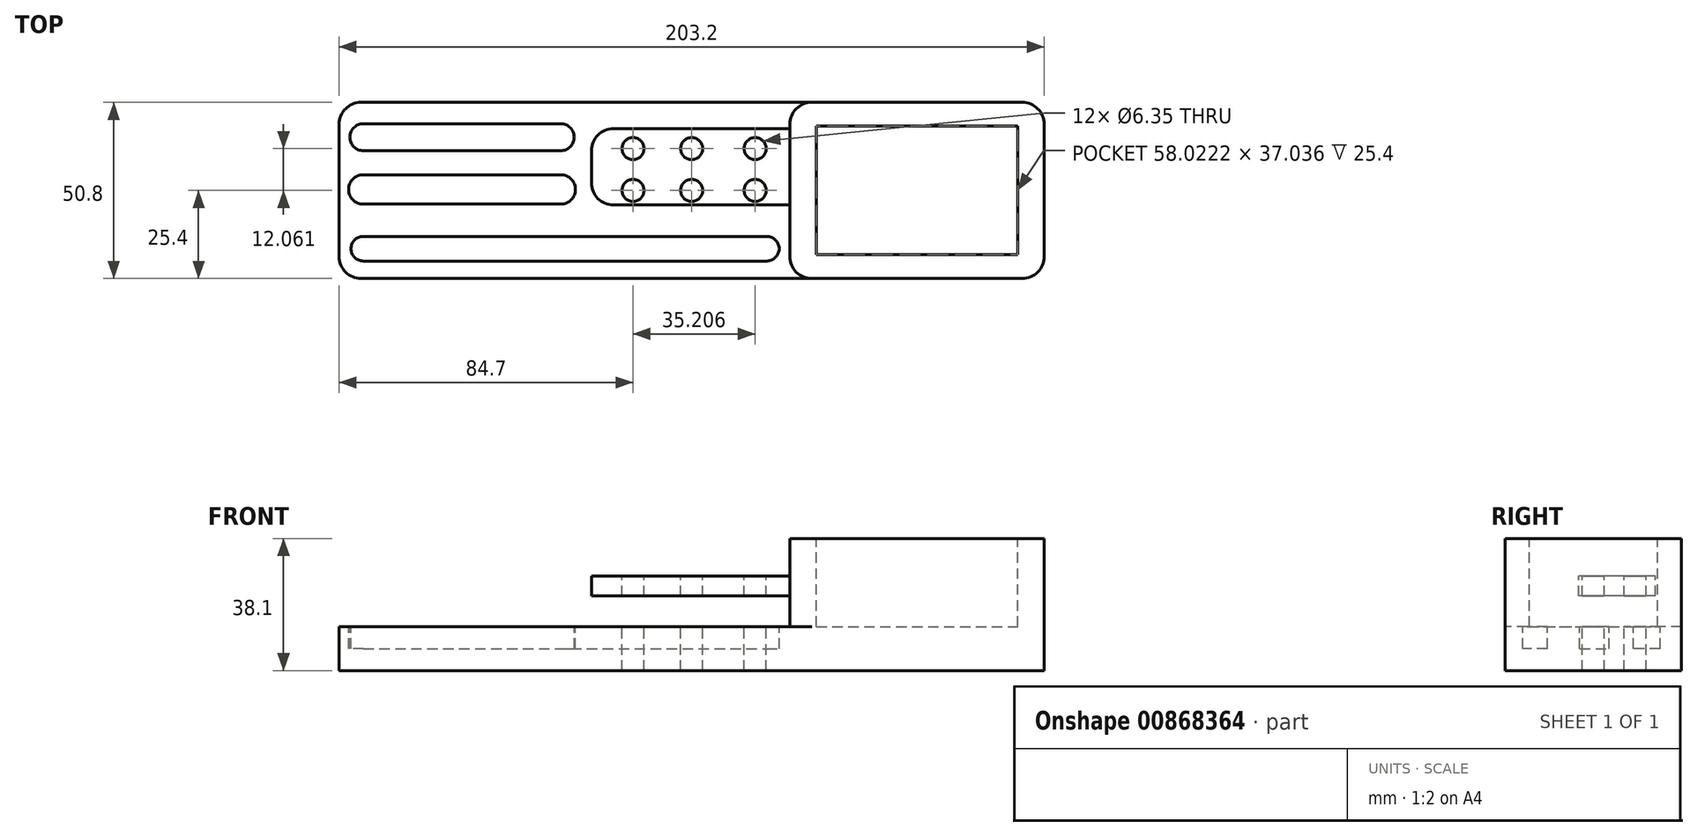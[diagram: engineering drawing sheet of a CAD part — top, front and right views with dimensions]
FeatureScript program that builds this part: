
annotation { "Feature Type Name" : "Feature", "Feature Type Description" : "" }
export const myFeature = defineFeature(function(context is Context, id is Id, definition is map)
    precondition{}
    {
        {
            var Q0;
            Q0=qCreatedBy(makeId("Top.planeOp"),FACE);
            var sketch = newSketch(context, id + "F0", { "sketchPlane" : qUnion([Q0])});
            skLineSegment(sketch, "E0.bottom", {"start": v(-101.6, -25.4) * mm, "end": v(101.6, -25.4) * mm});
            skLineSegment(sketch, "E0.top", {"start": v(-101.6, 25.4) * mm, "end": v(101.6, 25.4) * mm});
            skLineSegment(sketch, "E0.left", {"start": v(-101.6, -25.4) * mm, "end": v(-101.6, 25.4) * mm});
            skLineSegment(sketch, "E0.right", {"start": v(101.6, -25.4) * mm, "end": v(101.6, 25.4) * mm});
            skPoint(sketch, "E0.middle", {"position": v(0, 0) * mm});
            skLineSegment(sketch, "E1", {"start": v(45.35, 25.4) * mm, "end": v(45.35, -25.4) * mm});
            skSolve(sketch);
        }
        {
            var Q0;
            {var subQ0=sQuery(id+"F0.wireOp",EDGE,"E0.left");Q0=makeQuery(id+"F0.imprint","IMPRINT",FACE,{"disambiguationData":[TD([[makeQuery(id+"F0.imprint","IMPRINT",EDGE,{"derivedFrom":subQ0}),-1.0]])]});}
            var Q1;
            {var subQ0=sQuery(id+"F0.wireOp",EDGE,"E0.right");Q1=makeQuery(id+"F0.imprint","IMPRINT",FACE,{"disambiguationData":[TD([[makeQuery(id+"F0.imprint","IMPRINT",EDGE,{"derivedFrom":subQ0}),1.0]])]});}
            extrude(context, id + "F1", {"entities" : qUnion([Q0, Q1]), "depth" : 12.7 * mm, "offsetDistance" : 25.4 * mm});
        }
        {
            var Q0;
            Q0=makeQuery(id+"F1.opExtrude","CAP_FACE",FACE,{"disambiguationData":[OSD([sQuery(id+"F0.wireOp",EDGE,"E0.bottom"),sQuery(id+"F0.wireOp",EDGE,"E0.top"),sQuery(id+"F0.wireOp",EDGE,"E0.left"),sQuery(id+"F0.wireOp",EDGE,"E0.right")])],"isStart":false});
            var sketch = newSketch(context, id + "F2", { "sketchPlane" : qUnion([Q0])});
            skLineSegment(sketch, "E2", {"start": v(28.28, 25.4) * mm, "end": v(28.28, -25.4) * mm});
            skLineSegment(sketch, "E3", {"start": v(28.28, -25.4) * mm, "end": v(101.6, -25.4) * mm});
            skLineSegment(sketch, "E4", {"start": v(101.6, -25.4) * mm, "end": v(101.6, 25.4) * mm});
            skLineSegment(sketch, "E5", {"start": v(101.6, 25.4) * mm, "end": v(28.28, 25.4) * mm});
            skSolve(sketch);
        }
        {
            var Q0;
            Q0 = qSketchRegion(id + "F2", true);
            extrude(context, id + "F3", {"entities" : qUnion([Q0]), "operationType" : NewBodyOperationType.ADD, "depth" : 25.4 * mm, "offsetDistance" : 25.4 * mm});
        }
        {
            var Q0;
            Q0=makeQuery(id+"F3.opExtrude","CAP_FACE",FACE,{"disambiguationData":[OSD([sQuery(id+"F2.wireOp",EDGE,"E2"),sQuery(id+"F2.wireOp",EDGE,"E3"),sQuery(id+"F2.wireOp",EDGE,"E4"),sQuery(id+"F2.wireOp",EDGE,"E5")])],"isStart":false});
            var sketch = newSketch(context, id + "F4", { "sketchPlane" : qUnion([Q0])});
            skPoint(sketch, "E6", {"position": v(64.94, 0) * mm});
            skLineSegment(sketch, "E7.bottom", {"start": v(35.93, -18.52) * mm, "end": v(93.95, -18.52) * mm});
            skLineSegment(sketch, "E7.top", {"start": v(35.93, 18.52) * mm, "end": v(93.95, 18.52) * mm});
            skLineSegment(sketch, "E7.left", {"start": v(35.93, -18.52) * mm, "end": v(35.93, 18.52) * mm});
            skLineSegment(sketch, "E7.right", {"start": v(93.95, -18.52) * mm, "end": v(93.95, 18.52) * mm});
            skSolve(sketch);
        }
        {
            var Q0;
            Q0 = qSketchRegion(id + "F4", true);
            extrude(context, id + "F5", {"entities" : qUnion([Q0]), "operationType" : NewBodyOperationType.REMOVE, "oppositeDirection" : true, "depth" : 25.4 * mm, "offsetDistance" : 25.4 * mm});
        }
        {
            var Q0;
            Q0=makeQuery(id+"F1.opExtrude","CAP_FACE",FACE,{"disambiguationData":[OSD([sQuery(id+"F0.wireOp",EDGE,"E0.bottom"),sQuery(id+"F0.wireOp",EDGE,"E0.top"),sQuery(id+"F0.wireOp",EDGE,"E0.left"),sQuery(id+"F0.wireOp",EDGE,"E0.right")])],"isStart":false});
            var sketch = newSketch(context, id + "F6", { "sketchPlane" : qUnion([Q0])});
            skLineSegment(sketch, "E8.bottom", {"start": v(-94.61, 19.25) * mm, "end": v(-37.74, 19.25) * mm});
            skLineSegment(sketch, "E8.top", {"start": v(-94.61, 11.46) * mm, "end": v(-37.74, 11.46) * mm});
            skLineSegment(sketch, "E9.bottom", {"start": v(-94.61, 4.52) * mm, "end": v(-37.74, 4.52) * mm});
            skLineSegment(sketch, "E9.top", {"start": v(-94.61, -3.94) * mm, "end": v(-37.74, -3.94) * mm});
            skLineSegment(sketch, "E10.bottom", {"start": v(-94.61, -13.25) * mm, "end": v(21.67, -13.25) * mm});
            skLineSegment(sketch, "E10.top", {"start": v(-94.61, -20.36) * mm, "end": v(21.67, -20.36) * mm});
            skArc(sketch, "E11", {"start": v(-94.61, 19.25) * mm, "mid": v(-98.5, 15.35) * mm, "end": v(-94.61, 11.46) * mm});
            skArc(sketch, "E12", {"start": v(-37.74, 11.46) * mm, "mid": v(-33.85, 15.35) * mm, "end": v(-37.74, 19.25) * mm});
            skArc(sketch, "E13", {"start": v(-37.74, -3.94) * mm, "mid": v(-33.5, 0.29) * mm, "end": v(-37.74, 4.52) * mm});
            skArc(sketch, "E14", {"start": v(-94.61, 4.52) * mm, "mid": v(-98.84, 0.29) * mm, "end": v(-94.61, -3.94) * mm});
            skArc(sketch, "E15", {"start": v(-94.61, -13.25) * mm, "mid": v(-98.17, -16.8) * mm, "end": v(-94.61, -20.36) * mm});
            skArc(sketch, "E16", {"start": v(21.67, -20.36) * mm, "mid": v(25.22, -16.8) * mm, "end": v(21.67, -13.25) * mm});
            skSolve(sketch);
        }
        {
            var Q0;
            Q0 = qSketchRegion(id + "F6", true);
            extrude(context, id + "F7", {"entities" : qUnion([Q0]), "operationType" : NewBodyOperationType.REMOVE, "oppositeDirection" : true, "depth" : 6.35 * mm, "offsetDistance" : 25.4 * mm});
        }
        {
            var Q0;
            Q0=makeQuery(id+"F3.opExtrude","SWEPT_EDGE",EDGE,{"disambiguationData":[OSD([sQuery(id+"F0.wireOp",EDGE,"E0.bottom"),sQuery(id+"F2.wireOp",EDGE,"E2"),sQuery(id+"F2.wireOp",EDGE,"E3")])]});
            var Q1;
            Q1=makeQuery(id+"F3.opExtrude","SWEPT_EDGE",EDGE,{"disambiguationData":[OSD([sQuery(id+"F0.wireOp",EDGE,"E0.top"),sQuery(id+"F2.wireOp",EDGE,"E2"),sQuery(id+"F2.wireOp",EDGE,"E5")])]});
            var Q2;
            Q2=makeQuery(id+"F1.opExtrude","SWEPT_EDGE",EDGE,{"disambiguationData":[OSD([sQuery(id+"F0.wireOp",EDGE,"E0.bottom"),sQuery(id+"F0.wireOp",EDGE,"E0.left")])]});
            var Q3;
            Q3=makeQuery(id+"F1.opExtrude","SWEPT_EDGE",EDGE,{"disambiguationData":[OSD([sQuery(id+"F0.wireOp",EDGE,"E0.top"),sQuery(id+"F0.wireOp",EDGE,"E0.left")])]});
            var Q4;
            Q4=makeQuery(id+"F3.boolean.opBoolean","MERGE",EDGE,{"derivedFrom":[makeQuery(id+"F1.opExtrude","SWEPT_EDGE",EDGE,{"disambiguationData":[OSD([sQuery(id+"F0.wireOp",EDGE,"E0.top"),sQuery(id+"F0.wireOp",EDGE,"E0.right")])]}),makeQuery(id+"F3.opExtrude","SWEPT_EDGE",EDGE,{"disambiguationData":[OSD([sQuery(id+"F2.wireOp",EDGE,"E4"),sQuery(id+"F2.wireOp",EDGE,"E5")])]})]});
            var Q5;
            Q5=makeQuery(id+"F3.boolean.opBoolean","MERGE",EDGE,{"derivedFrom":[makeQuery(id+"F1.opExtrude","SWEPT_EDGE",EDGE,{"disambiguationData":[OSD([sQuery(id+"F0.wireOp",EDGE,"E0.bottom"),sQuery(id+"F0.wireOp",EDGE,"E0.right")])]}),makeQuery(id+"F3.opExtrude","SWEPT_EDGE",EDGE,{"disambiguationData":[OSD([sQuery(id+"F2.wireOp",EDGE,"E3"),sQuery(id+"F2.wireOp",EDGE,"E4")])]})]});
            fillet(context, id + "F8", {"entities" : qUnion([Q0, Q1, Q2, Q3, Q4, Q5]), "radius" : 6.35 * mm, "tangentPropagation" : true, "allowEdgeOverflow" : false});
        }
        {
            var Q0;
            Q0=makeQuery(id+"F3.opExtrude","SWEPT_FACE",FACE,{"disambiguationData":[OSD([sQuery(id+"F2.wireOp",EDGE,"E2")])]});
            var sketch = newSketch(context, id + "F9", { "sketchPlane" : qUnion([Q0])});
            skLineSegment(sketch, "E17.bottom", {"start": v(-17.81, 21.53) * mm, "end": v(4.19, 21.53) * mm});
            skLineSegment(sketch, "E17.top", {"start": v(-17.81, 27.28) * mm, "end": v(4.19, 27.28) * mm});
            skLineSegment(sketch, "E17.left", {"start": v(-17.81, 21.53) * mm, "end": v(-17.81, 27.28) * mm});
            skLineSegment(sketch, "E17.right", {"start": v(4.19, 21.53) * mm, "end": v(4.19, 27.28) * mm});
            skPoint(sketch, "E17.middle", {"position": v(-6.81, 24.4) * mm});
            skSolve(sketch);
        }
        {
            var Q0;
            Q0 = qSketchRegion(id + "F9", true);
            extrude(context, id + "F10", {"entities" : qUnion([Q0]), "operationType" : NewBodyOperationType.ADD, "depth" : 57.15 * mm, "offsetDistance" : 25.4 * mm});
        }
        {
            var Q0;
            Q0=makeQuery(id+"F10.opExtrude","CAP_EDGE",EDGE,{"disambiguationData":[OSD([sQuery(id+"F9.wireOp",EDGE,"E17.right")])],"isStart":false});
            var Q1;
            Q1=makeQuery(id+"F10.opExtrude","CAP_EDGE",EDGE,{"disambiguationData":[OSD([sQuery(id+"F9.wireOp",EDGE,"E17.left")])],"isStart":false});
            fillet(context, id + "F11", {"entities" : qUnion([Q0, Q1]), "radius" : 6.35 * mm, "tangentPropagation" : true, "allowEdgeOverflow" : false});
        }
        {
            var Q0;
            Q0=makeQuery(id+"F10.opExtrude","SWEPT_FACE",FACE,{"disambiguationData":[OSD([sQuery(id+"F9.wireOp",EDGE,"E17.top")])]});
            var sketch = newSketch(context, id + "F12", { "sketchPlane" : qUnion([Q0])});
            skPoint(sketch, "E18", {"position": v(-16.9, 12.06) * mm});
            skPoint(sketch, "E19", {"position": v(0, 12.06) * mm});
            skPoint(sketch, "E20", {"position": v(18.3, 12.06) * mm});
            skPoint(sketch, "E21", {"position": v(18.3, 0) * mm});
            skPoint(sketch, "E22", {"position": v(0, 0) * mm});
            skPoint(sketch, "E23", {"position": v(-16.9, 0) * mm});
            skSolve(sketch);
        }
        {
            var Q0;
            Q0=sQuery(id+"F12.wireOp",VERTEX,"E18");
            var Q1;
            Q1=sQuery(id+"F12.wireOp",VERTEX,"E19");
            var Q2;
            Q2=sQuery(id+"F12.wireOp",VERTEX,"E20");
            var Q3;
            Q3=sQuery(id+"F12.wireOp",VERTEX,"E21");
            var Q4;
            Q4=sQuery(id+"F12.wireOp",VERTEX,"E22");
            var Q5;
            Q5=sQuery(id+"F12.wireOp",VERTEX,"E23");
            var Q6;
            Q6=makeQuery(id+"F1.opExtrude","SWEPT_BODY",BODY,{"disambiguationData":[OSD([sQuery(id+"F0.wireOp",EDGE,"E0.bottom"),sQuery(id+"F0.wireOp",EDGE,"E0.top"),sQuery(id+"F0.wireOp",EDGE,"E0.left"),sQuery(id+"F0.wireOp",EDGE,"E0.right")])]});
            hole(context, id + "F13", {"style" : HoleStyle.SIMPLE, "endStyle" : HoleEndStyle.THROUGH, "holeDiameter" : 6.35 * mm, "majorDiameter" : 6.35 * mm, "isTappedThrough" : true, "tappedDepth" : 12.7 * mm, "tapClearance" : 3, "locations" : qUnion([Q0, Q1, Q2, Q3, Q4, Q5]), "scope" : qUnion([Q6])});
        }
    });
